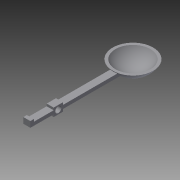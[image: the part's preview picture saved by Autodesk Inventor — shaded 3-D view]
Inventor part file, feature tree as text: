
AUTODESK INVENTOR PART (.ipt)
format: ipt  version: 2015 (Build 190159000, 159)  size: 145,408 bytes
history: native  units: in
note: dims shown in document units (in); Inventor stores cm internally (conversion verified against a paired STEP export)
features: sketch x7, extrude x5, revolve x1, plane x1, hole x1, projected_geometry x1
ambient origin geometry x8: Origin, YZ Plane, XZ Plane, XY Plane, X Axis, Y Axis, Z Axis, Center Point
bodies: Solid1 (feature_tree)
feature tree (16):
  revolve  "Revolution1"  [1 undecoded]
  plane  "Work Plane1"
  extrude  "Extrusion1"  Depth=0.25in
  extrude  "Extrusion2"  Depth=0.425in
  extrude  "Extrusion3"  Depth=0.075in
  sketch  "Sketch6"  dims[d14=0.075in d15=0.025in]
  extrude  "Extrusion4"  Depth=0.025in
  hole  "Hole1"  [1 undecoded]
  extrude  "Extrusion5"  Depth=0.05in
  sketch  "Sketch2"  dims[d4=1.0in d5=0.9in]
  sketch  "Sketch3"  dims[d8=180.0deg d9=0.25in]
  sketch  "Sketch4"  dims[d10=0.433in d11=0.425in]
  projected_geometry  "Projected Loop1"
  sketch  "Sketch5"  dims[d12=0.075in d13=0.075in]
  sketch  "Sketch7"  dims[d16=1.85in d17=0.069in d18=0.0in d19=0.0in d20=0.04in d21=0.0in]
  sketch  "Sketch8"  dims[d22=0.04in d23=0.0in d24=0.0375in d25=0.6in d26=0.6in d27=0.1in d28=0.1in d29=0.05in d30=0.125in d31=0.0in d32=0.0in d33=0.13in d34=0.75in d35=0.375in d36=0.25in d37=0.5635in d38=1.0in d39=0.8108in d40=0.075in d41=0.05in d42=0.0in]
note: 2 required parameter values undecoded (feature->parameter linkage not recoverable at this tier; creation-order binding heuristic only, values carry confidence <= 0.55)